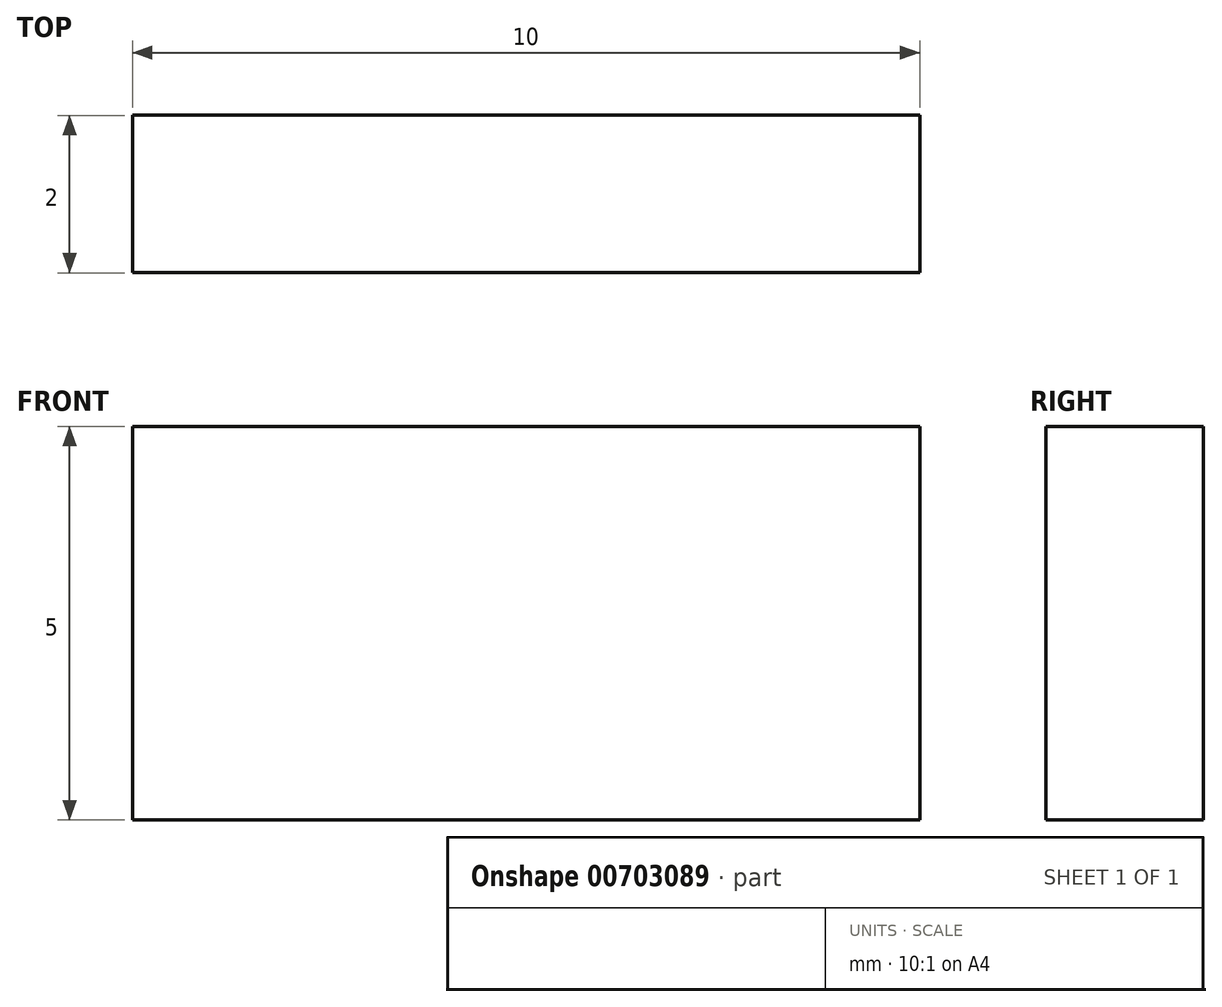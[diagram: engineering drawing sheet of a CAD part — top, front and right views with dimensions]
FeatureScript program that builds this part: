
annotation { "Feature Type Name" : "Feature", "Feature Type Description" : "" }
export const myFeature = defineFeature(function(context is Context, id is Id, definition is map)
    precondition{}
    {
        {
            var Q0;
            Q0=qCreatedBy(makeId("Top.planeOp"),FACE);
            var sketch = newSketch(context, id + "F0", { "sketchPlane" : qUnion([Q0])});
            skLineSegment(sketch, "E0.bottom", {"start": v(-7.56, 1.27) * mm, "end": v(2.44, 1.27) * mm});
            skLineSegment(sketch, "E0.top", {"start": v(-7.56, -0.73) * mm, "end": v(2.44, -0.73) * mm});
            skLineSegment(sketch, "E0.left", {"start": v(-7.56, 1.27) * mm, "end": v(-7.56, -0.73) * mm});
            skLineSegment(sketch, "E0.right", {"start": v(2.44, 1.27) * mm, "end": v(2.44, -0.73) * mm});
            skSolve(sketch);
        }
        {
            var Q0;
            Q0=makeQuery(id+"F0.imprint","IMPRINT",FACE,{"disambiguationData":[TD([[makeQuery(id+"F0.imprint","IMPRINT",EDGE,{"derivedFrom":sQuery(id+"F0.wireOp",EDGE,"E0.bottom")}),-1.0]])]});
            extrude(context, id + "F1", {"entities" : qUnion([Q0]), "depth" : 5 * mm, "offsetDistance" : 25 * mm});
        }
    });
